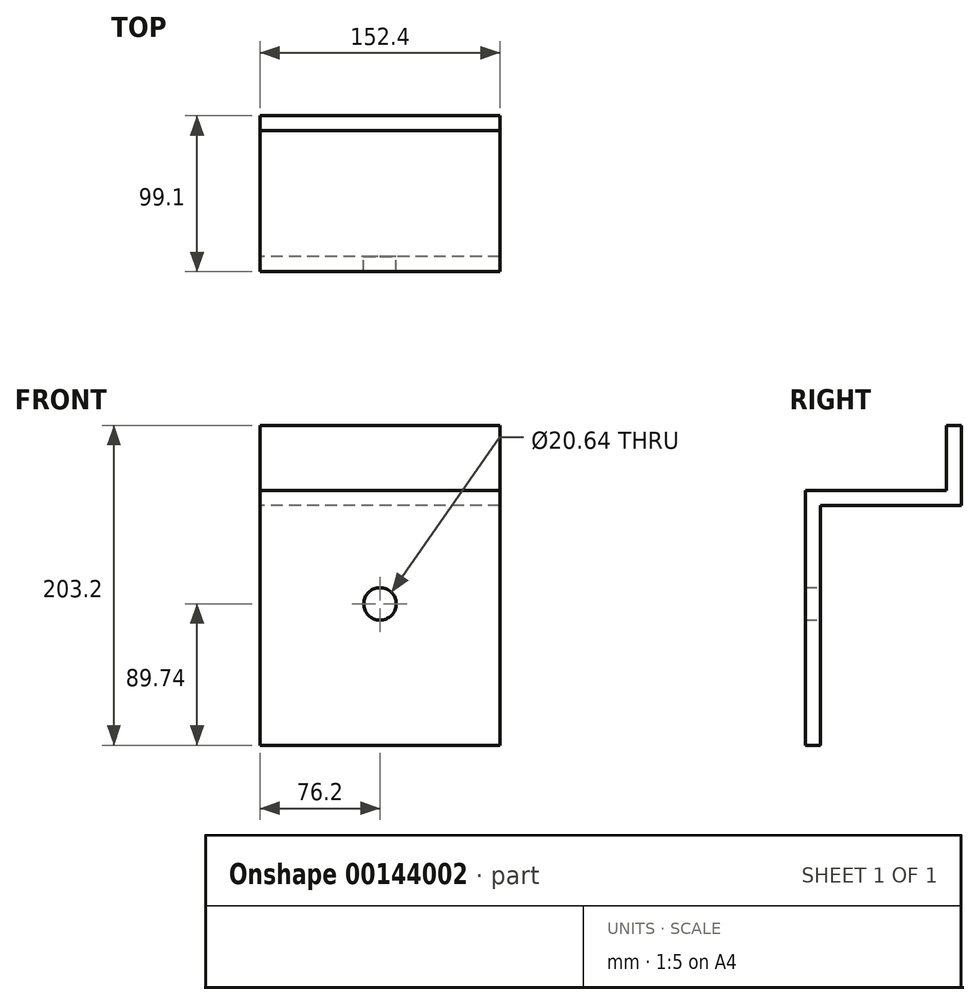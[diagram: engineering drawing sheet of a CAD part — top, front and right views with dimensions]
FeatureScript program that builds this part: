
annotation { "Feature Type Name" : "Feature", "Feature Type Description" : "" }
export const myFeature = defineFeature(function(context is Context, id is Id, definition is map)
    precondition{}
    {
        {
            var Q0;
            Q0=qCreatedBy(makeId("Right.planeOp"),FACE);
            var sketch = newSketch(context, id + "F0", { "sketchPlane" : qUnion([Q0])});
            skLineSegment(sketch, "E0", {"start": v(0, -89.74) * mm, "end": v(0, 72.19) * mm});
            skLineSegment(sketch, "E1", {"start": v(0, 72.19) * mm, "end": v(89.57, 72.19) * mm});
            skLineSegment(sketch, "E2", {"start": v(89.57, 72.19) * mm, "end": v(89.57, 113.46) * mm});
            skLineSegment(sketch, "E3", {"start": v(89.57, 113.46) * mm, "end": v(99.1, 113.46) * mm});
            skLineSegment(sketch, "E4", {"start": v(99.1, 113.46) * mm, "end": v(99.1, 62.66) * mm});
            skLineSegment(sketch, "E5", {"start": v(99.1, 62.66) * mm, "end": v(9.52, 62.66) * mm});
            skLineSegment(sketch, "E6", {"start": v(9.52, 62.66) * mm, "end": v(9.52, -89.74) * mm});
            skLineSegment(sketch, "E7", {"start": v(9.52, -89.74) * mm, "end": v(0, -89.74) * mm});
            skSolve(sketch);
        }
        {
            var Q0;
            Q0 = qSketchRegion(id + "F0", true);
            extrude(context, id + "F1", {"entities" : qUnion([Q0]), "endBound" : BoundingType.SYMMETRIC, "depth" : 152.4 * mm});
        }
        {
            var Q0;
            Q0=makeQuery(id+"F1.opExtrude","SWEPT_FACE",FACE,{"disambiguationData":[OSD([sQuery(id+"F0.wireOp",EDGE,"E6")])]});
            var sketch = newSketch(context, id + "F2", { "sketchPlane" : qUnion([Q0])});
            skCircle(sketch, "E8", {"center": v(0, 0) * mm, "radius": 10.32 * mm});
            skSolve(sketch);
        }
        {
            var Q0;
            Q0=makeQuery(id+"F2.imprint","IMPRINT",FACE,{"disambiguationData":[TD([[makeQuery(id+"F2.imprint","IMPRINT",EDGE,{"derivedFrom":sQuery(id+"F2.wireOp",EDGE,"E8")}),1.0]])]});
            var Q1;
            Q1=makeQuery(id+"F1.opExtrude","SWEPT_FACE",FACE,{"disambiguationData":[OSD([sQuery(id+"F0.wireOp",EDGE,"E0")])]});
            extrude(context, id + "F3", {"entities" : qUnion([Q0]), "operationType" : NewBodyOperationType.REMOVE, "endBound" : BoundingType.UP_TO_SURFACE, "oppositeDirection" : true, "endBoundEntityFace" : qUnion([Q1]), "depth" : 25.4 * mm});
        }
    });
